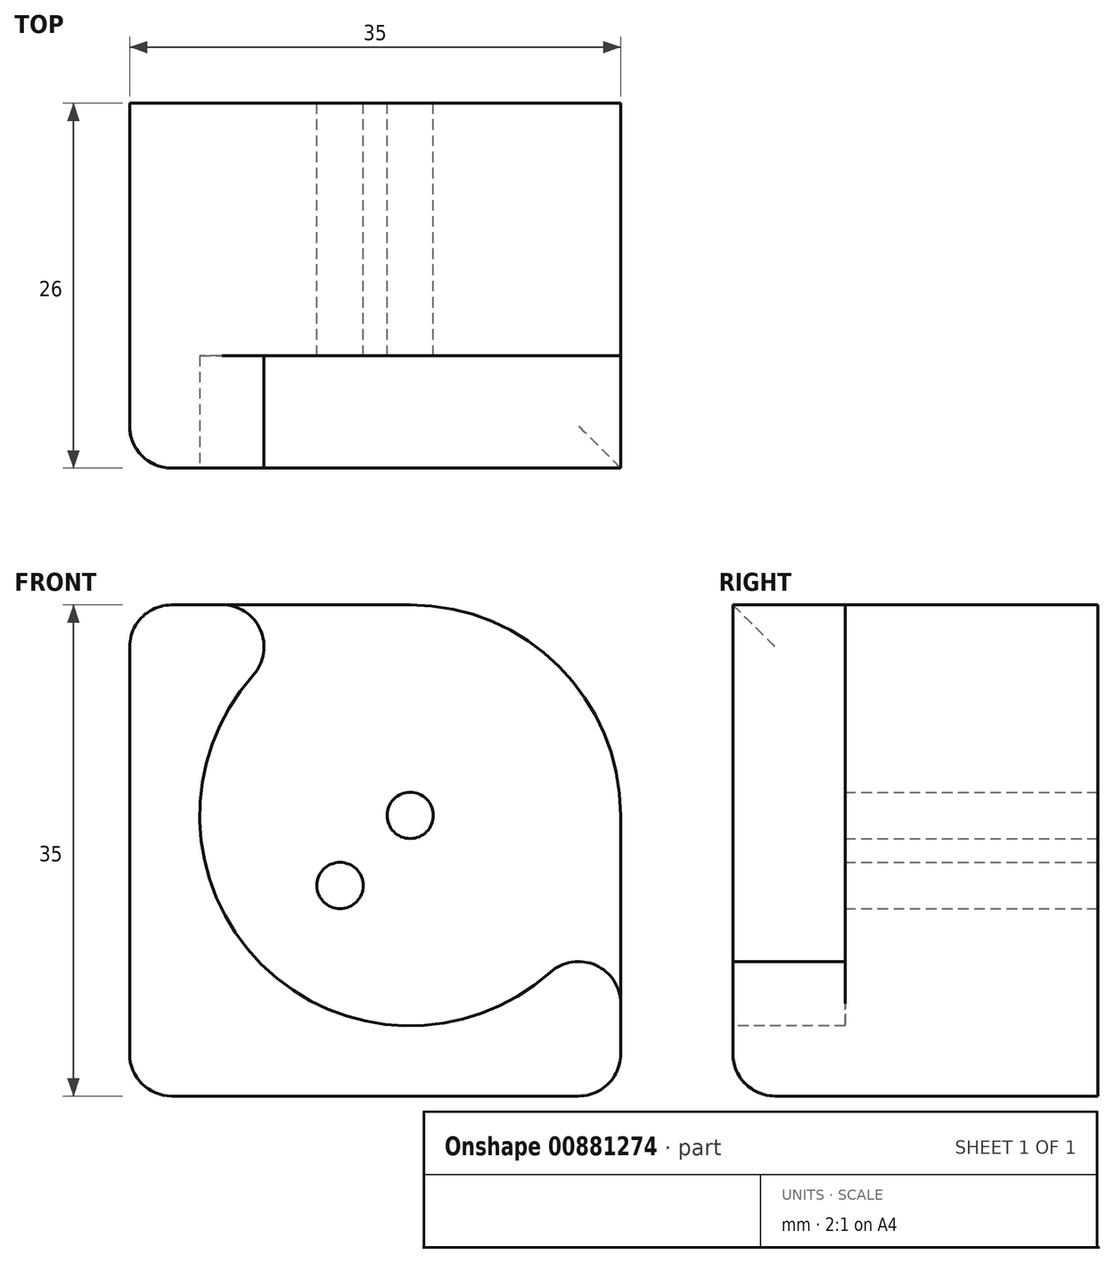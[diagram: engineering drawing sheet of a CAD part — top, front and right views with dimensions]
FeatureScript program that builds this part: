
annotation { "Feature Type Name" : "Feature", "Feature Type Description" : "" }
export const myFeature = defineFeature(function(context is Context, id is Id, definition is map)
    precondition{}
    {
        {
            var Q0;
            Q0=qCreatedBy(makeId("Front.planeOp"),FACE);
            var sketch = newSketch(context, id + "F0", { "sketchPlane" : qUnion([Q0])});
            skLineSegment(sketch, "E0", {"start": v(-35, 0) * mm, "end": v(-35, 35) * mm});
            skLineSegment(sketch, "E1", {"start": v(-35, 35) * mm, "end": v(0, 35) * mm});
            skLineSegment(sketch, "E2", {"start": v(0, 35) * mm, "end": v(0, 0) * mm});
            skLineSegment(sketch, "E3", {"start": v(-35, 0) * mm, "end": v(0, 0) * mm});
            skLineSegment(sketch, "E4", {"start": v(0, 35) * mm, "end": v(-15, 35) * mm});
            skLineSegment(sketch, "E5", {"start": v(-15, 35) * mm, "end": v(-15, 20) * mm});
            skCircle(sketch, "E6", {"center": v(-15, 20) * mm, "radius": 15 * mm});
            skPoint(sketch, "E7.endSnap0", {"position": v(-35, 17.5) * mm});
            skLineSegment(sketch, "E8", {"start": v(-35, 0) * mm, "end": v(-20, 0) * mm});
            skLineSegment(sketch, "E9", {"start": v(-20, 0) * mm, "end": v(-20, 15) * mm});
            skSolve(sketch);
        }
        {
            var Q0;
            {var subQ5=sQuery(id+"F0.wireOp",EDGE,"E0");Q0=makeQuery(id+"F0.imprint","IMPRINT",FACE,{"disambiguationData":[TD([[makeQuery(id+"F0.imprint","IMPRINT",EDGE,{"derivedFrom":subQ5}),-1.0]])]});}
            var Q1;
            {var subQ0=sQuery(id+"F0.wireOp",EDGE,"E3");var subQ1=sQuery(id+"F0.wireOp",EDGE,"E2");var subQ2=makeQuery(id+"F0.imprint","INTERSECT",VERTEX,{"derivedFrom":[subQ1,subQ0]});Q1=makeQuery(id+"F0.imprint","IMPRINT",FACE,{"disambiguationData":[TD([[makeQuery(id+"F0.imprint","IMPRINT",EDGE,{"disambiguationData":[TD([[subQ2,1.0]])],"derivedFrom":subQ1}),-1.0]])]});}
            var Q2;
            {var subQ0=sQuery(id+"F0.wireOp",EDGE,"E6");var subQ2=makeQuery(id+"F0.imprint","INTERSECT",VERTEX,{"derivedFrom":[sQuery(id+"F0.wireOp",EDGE,"E2"),subQ0]});Q2=makeQuery(id+"F0.imprint","IMPRINT",FACE,{"disambiguationData":[TD([[makeQuery(id+"F0.imprint","IMPRINT",EDGE,{"disambiguationData":[TD([[subQ2,1.0]])],"derivedFrom":subQ0}),1.0]])]});}
            extrude(context, id + "F1", {"entities" : qUnion([Q0, Q1, Q2]), "oppositeDirection" : true, "depth" : 26 * mm, "offsetDistance" : 25 * mm});
        }
        {
            var Q0;
            {var subQ0=sQuery(id+"F0.wireOp",EDGE,"E6");var subQ2=makeQuery(id+"F0.imprint","INTERSECT",VERTEX,{"derivedFrom":[sQuery(id+"F0.wireOp",EDGE,"E2"),subQ0]});Q0=makeQuery(id+"F0.imprint","IMPRINT",FACE,{"disambiguationData":[TD([[makeQuery(id+"F0.imprint","IMPRINT",EDGE,{"disambiguationData":[TD([[subQ2,1.0]])],"derivedFrom":subQ0}),1.0]])]});}
            extrude(context, id + "F2", {"entities" : qUnion([Q0]), "operationType" : NewBodyOperationType.REMOVE, "oppositeDirection" : true, "depth" : 8 * mm, "offsetDistance" : 25 * mm});
        }
        {
            var Q0;
            Q0=sQuery(id+"F0.wireOp",VERTEX,"E7.end");
            var Q1;
            Q1=sQuery(id+"F0.wireOp",VERTEX,"E5.end");
            var Q2;
            Q2=sQuery(id+"F0.wireOp",VERTEX,"E9.end");
            var Q3;
            Q3=makeQuery(id+"F1.opExtrude","SWEPT_BODY",BODY,{"disambiguationData":[OSD([sQuery(id+"F0.wireOp",EDGE,"E0"),sQuery(id+"F0.wireOp",EDGE,"E1"),sQuery(id+"F0.wireOp",EDGE,"E2"),sQuery(id+"F0.wireOp",EDGE,"E3"),sQuery(id+"F0.wireOp",EDGE,"E6")])]});
            hole(context, id + "F3", {"style" : HoleStyle.SIMPLE, "endStyle" : HoleEndStyle.BLIND, "holeDiameter" : 3.3 * mm, "majorDiameter" : 5 * mm, "holeDepth" : 30 * mm, "isTappedThrough" : true, "tappedDepth" : 12 * mm, "tapClearance" : 3, "locations" : qUnion([Q0, Q1, Q2]), "scope" : qUnion([Q3]), "startStyle" : HoleStartStyle.PART});
        }
        {
            var Q0;
            Q0=makeQuery(id+"F1.opExtrude","SWEPT_EDGE",EDGE,{"disambiguationData":[OSD([sQuery(id+"F0.wireOp",EDGE,"E0"),sQuery(id+"F0.wireOp",EDGE,"E1")])]});
            var Q1;
            Q1=makeQuery(id+"F1.opExtrude","CAP_EDGE",EDGE,{"disambiguationData":[OSD([sQuery(id+"F0.wireOp",EDGE,"E0")])],"isStart":true});
            var Q2;
            Q2=makeQuery(id+"F1.opExtrude","CAP_EDGE",EDGE,{"disambiguationData":[OSD([sQuery(id+"F0.wireOp",EDGE,"E3")])],"isStart":true});
            var Q3;
            Q3=makeQuery(id+"F1.opExtrude","SWEPT_EDGE",EDGE,{"disambiguationData":[OSD([sQuery(id+"F0.wireOp",EDGE,"E0"),sQuery(id+"F0.wireOp",EDGE,"E3")])]});
            var Q4;
            Q4=makeQuery(id+"F1.opExtrude","SWEPT_EDGE",EDGE,{"disambiguationData":[OSD([sQuery(id+"F0.wireOp",EDGE,"E2"),sQuery(id+"F0.wireOp",EDGE,"E3")])]});
            var Q5;
            {var subQ0=sQuery(id+"F0.wireOp",EDGE,"E2");var subQ1=sQuery(id+"F0.wireOp",EDGE,"E6");Q5=makeQuery(id+"F2.boolean.opBoolean","SPLIT",EDGE,{"disambiguationData":[topologyDisambiguationEdgeConnected([makeQuery(id+"F2.opExtrude","SWEPT_FACE",FACE,{"disambiguationData":[OSD([subQ1])]})])],"derivedFrom":makeQuery(id+"F1.opExtrude","SWEPT_EDGE",EDGE,{"disambiguationData":[OSD([subQ0,subQ1])]})});}
            var Q6;
            {var subQ0=sQuery(id+"F0.wireOp",EDGE,"E1");var subQ1=sQuery(id+"F0.wireOp",EDGE,"E6");Q6=makeQuery(id+"F2.boolean.opBoolean","SPLIT",EDGE,{"disambiguationData":[topologyDisambiguationEdgeConnected([makeQuery(id+"F2.opExtrude","SWEPT_FACE",FACE,{"disambiguationData":[OSD([subQ1])]})])],"derivedFrom":makeQuery(id+"F1.opExtrude","SWEPT_EDGE",EDGE,{"disambiguationData":[OSD([subQ0,sQuery(id+"F0.wireOp",EDGE,"E4"),subQ1])]})});}
            fillet(context, id + "F4", {"entities" : qUnion([Q0, Q1, Q2, Q3, Q4, Q5, Q6]), "radius" : 3 * mm, "tangentPropagation" : true, "allowEdgeOverflow" : false});
        }
    });
